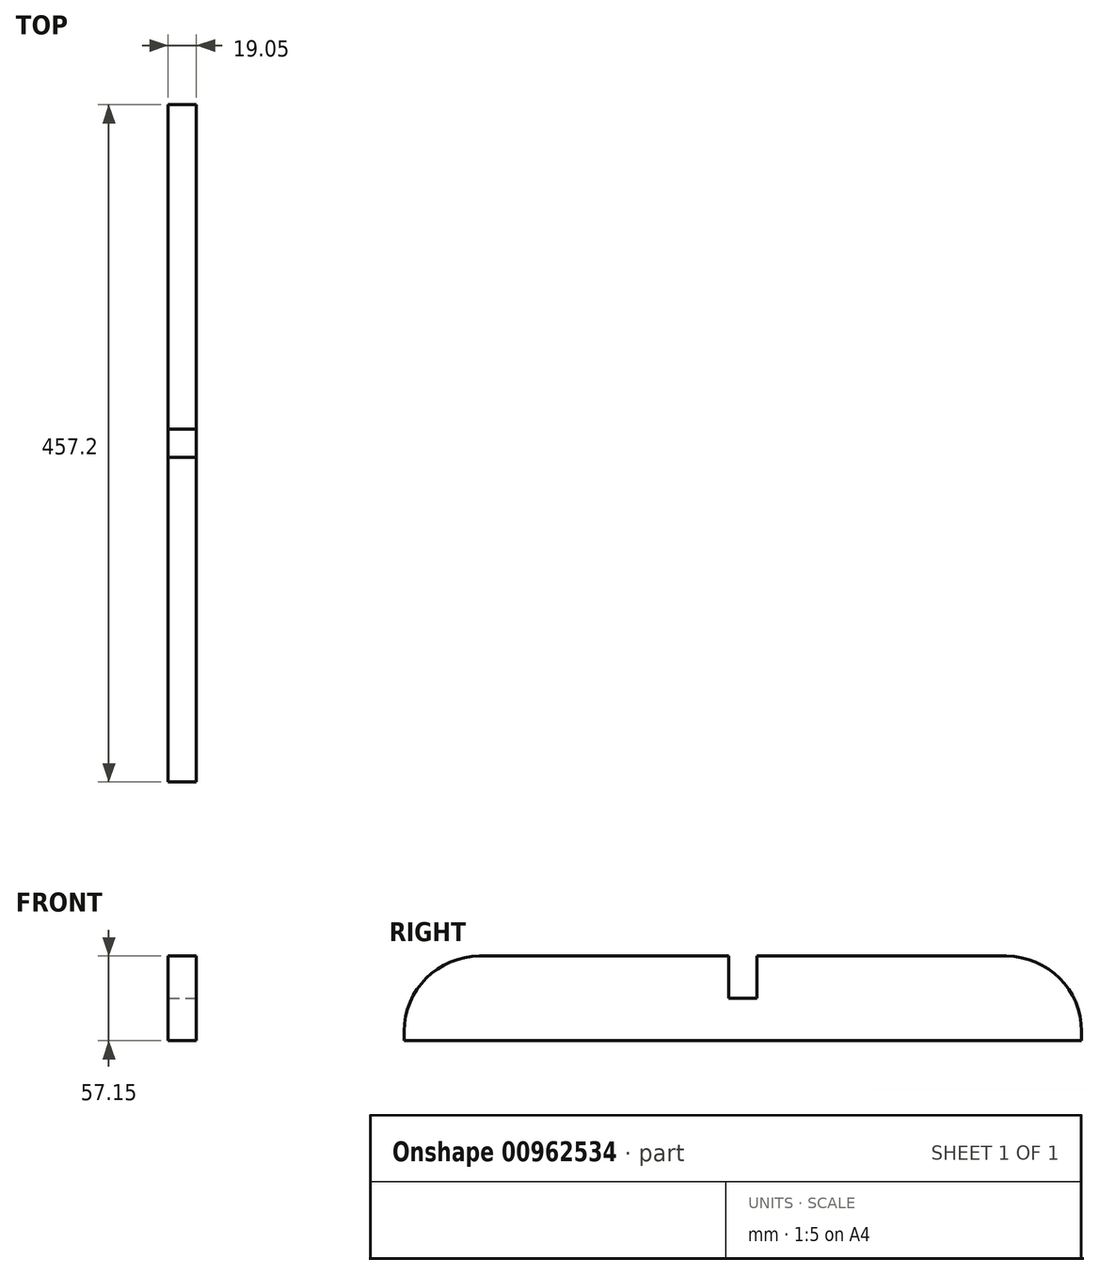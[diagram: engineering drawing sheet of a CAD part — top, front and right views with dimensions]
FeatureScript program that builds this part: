
annotation { "Feature Type Name" : "Feature", "Feature Type Description" : "" }
export const myFeature = defineFeature(function(context is Context, id is Id, definition is map)
    precondition{}
    {
        {
            var Q0;
            Q0=qCreatedBy(makeId("Front.planeOp"),FACE);
            var sketch = newSketch(context, id + "F0", { "sketchPlane" : qUnion([Q0])});
            skLineSegment(sketch, "E0.bottom", {"start": v(0, 0) * mm, "end": v(19.05, 0) * mm});
            skLineSegment(sketch, "E0.top", {"start": v(0, 57.15) * mm, "end": v(19.05, 57.15) * mm});
            skLineSegment(sketch, "E0.left", {"start": v(0, 0) * mm, "end": v(0, 57.15) * mm});
            skLineSegment(sketch, "E0.right", {"start": v(19.05, 0) * mm, "end": v(19.05, 57.15) * mm});
            skSolve(sketch);
        }
        {
            var Q0;
            Q0=makeQuery(id+"F0.imprint","IMPRINT",FACE,{"disambiguationData":[TD([[makeQuery(id+"F0.imprint","IMPRINT",EDGE,{"derivedFrom":sQuery(id+"F0.wireOp",EDGE,"E0.bottom")}),1.0]])]});
            extrude(context, id + "F1", {"entities" : qUnion([Q0]), "depth" : 457.2 * mm, "offsetDistance" : 25.4 * mm});
        }
        {
            var Q0;
            Q0=makeQuery(id+"F1.opExtrude","SWEPT_FACE",FACE,{"disambiguationData":[OSD([sQuery(id+"F0.wireOp",EDGE,"E0.right")])]});
            var sketch = newSketch(context, id + "F2", { "sketchPlane" : qUnion([Q0])});
            skLineSegment(sketch, "E1", {"start": v(-228.6, 57.15) * mm, "end": v(-228.6, 0) * mm, "construction": true});
            skPoint(sketch, "E2", {"position": v(-228.6, 28.58) * mm});
            skLineSegment(sketch, "E3", {"start": v(-238.13, 28.58) * mm, "end": v(-219.08, 28.58) * mm});
            skLineSegment(sketch, "E4", {"start": v(-238.13, 28.58) * mm, "end": v(-238.13, 57.15) * mm});
            skLineSegment(sketch, "E5", {"start": v(-238.13, 57.15) * mm, "end": v(-219.08, 57.15) * mm});
            skLineSegment(sketch, "E6", {"start": v(-219.08, 57.15) * mm, "end": v(-219.08, 28.58) * mm});
            skSolve(sketch);
        }
        {
            var Q0;
            Q0=makeQuery(id+"F2.imprint","IMPRINT",FACE,{"disambiguationData":[TD([[makeQuery(id+"F2.imprint","IMPRINT",EDGE,{"derivedFrom":sQuery(id+"F2.wireOp",EDGE,"E3")}),1.0]])]});
            extrude(context, id + "F3", {"entities" : qUnion([Q0]), "operationType" : NewBodyOperationType.REMOVE, "endBound" : BoundingType.UP_TO_NEXT, "oppositeDirection" : true, "depth" : 25.4 * mm, "offsetDistance" : 25.4 * mm});
        }
        {
            var Q0;
            Q0=makeQuery(id+"F1.opExtrude","CAP_EDGE",EDGE,{"disambiguationData":[OSD([sQuery(id+"F0.wireOp",EDGE,"E0.top")])],"isStart":true});
            var Q1;
            Q1=makeQuery(id+"F1.opExtrude","CAP_EDGE",EDGE,{"disambiguationData":[OSD([sQuery(id+"F0.wireOp",EDGE,"E0.top")])],"isStart":false});
            fillet(context, id + "F4", {"entities" : qUnion([Q0, Q1]), "radius" : 50.8 * mm, "tangentPropagation" : true, "allowEdgeOverflow" : false});
        }
    });
